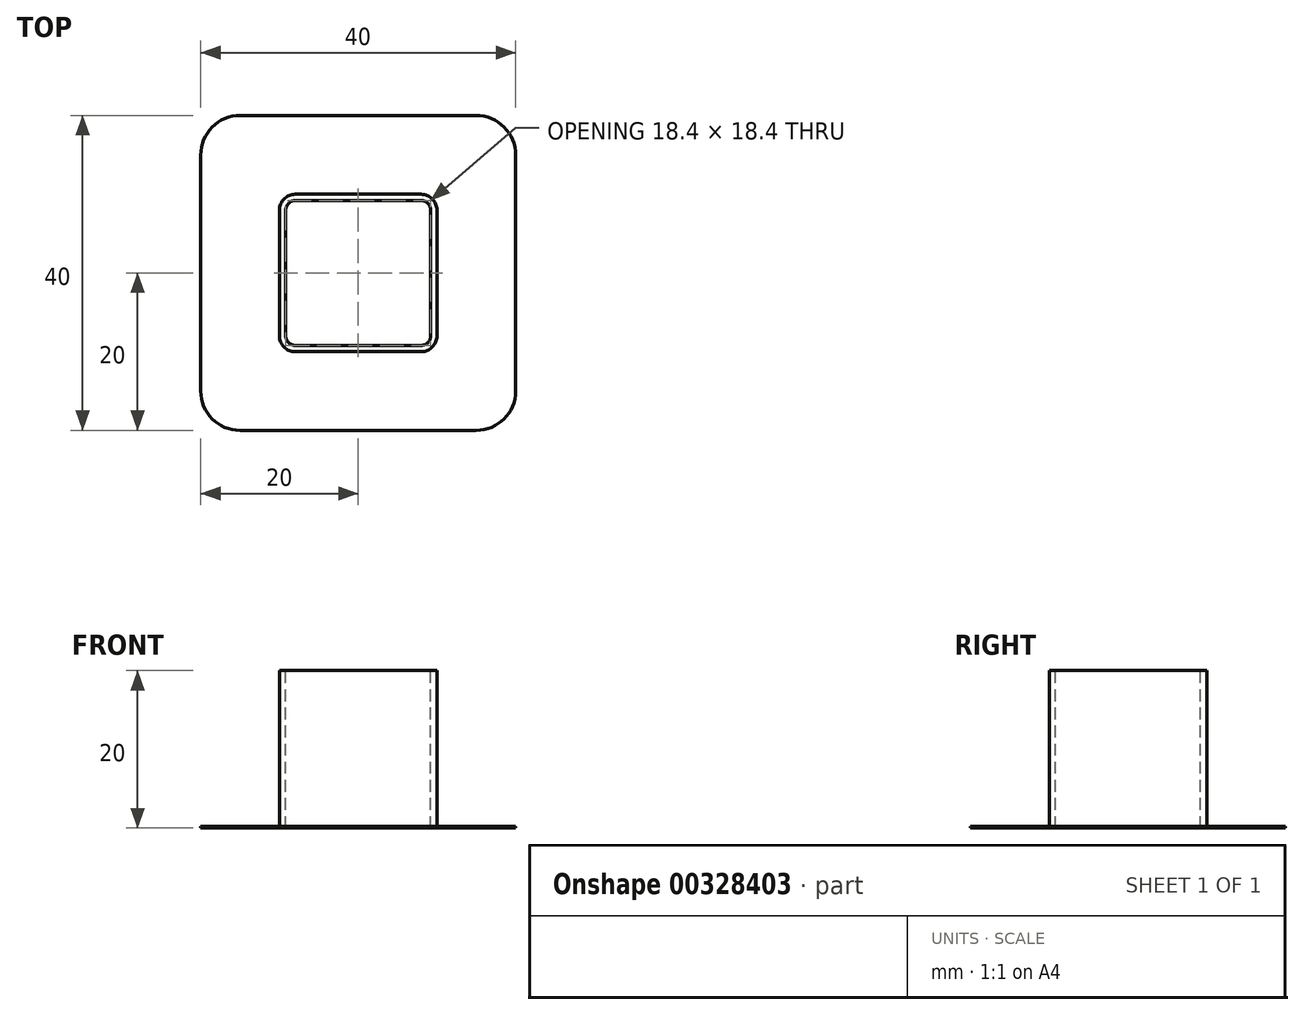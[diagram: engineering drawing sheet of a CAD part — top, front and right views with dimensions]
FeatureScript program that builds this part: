
annotation { "Feature Type Name" : "Feature", "Feature Type Description" : "" }
export const myFeature = defineFeature(function(context is Context, id is Id, definition is map)
    precondition{}
    {
        {
            var Q0;
            Q0=qCreatedBy(makeId("Top.planeOp"),FACE);
            var sketch = newSketch(context, id + "F0", { "sketchPlane" : qUnion([Q0])});
            skLineSegment(sketch, "E0.bottom", {"start": v(-8, 10) * mm, "end": v(8, 10) * mm});
            skLineSegment(sketch, "E0.top", {"start": v(-8, -10) * mm, "end": v(8, -10) * mm});
            skLineSegment(sketch, "E0.left", {"start": v(-10, 8) * mm, "end": v(-10, -8) * mm});
            skLineSegment(sketch, "E0.right", {"start": v(10, 8) * mm, "end": v(10, -8) * mm});
            skPoint(sketch, "E1", {"position": v(0, 10) * mm});
            skPoint(sketch, "E2", {"position": v(10, 0) * mm});
            skPoint(sketch, "E3.visualSharp", {"position": v(-10, 10) * mm});
            skArc(sketch, "E3.filletArc", {"start": v(-8, 10) * mm, "mid": v(-9.41, 9.41) * mm, "end": v(-10, 8) * mm});
            skPoint(sketch, "E4.visualSharp", {"position": v(10, 10) * mm});
            skArc(sketch, "E4.filletArc", {"start": v(10, 8) * mm, "mid": v(9.41, 9.41) * mm, "end": v(8, 10) * mm});
            skPoint(sketch, "E5.visualSharp", {"position": v(10, -10) * mm});
            skArc(sketch, "E5.filletArc", {"start": v(8, -10) * mm, "mid": v(9.41, -9.41) * mm, "end": v(10, -8) * mm});
            skPoint(sketch, "E6.visualSharp", {"position": v(-10, -10) * mm});
            skArc(sketch, "E6.filletArc", {"start": v(-10, -8) * mm, "mid": v(-9.41, -9.41) * mm, "end": v(-8, -10) * mm});
            skSolve(sketch);
        }
        {
            var Q0;
            Q0=makeQuery(id+"F0.imprint","IMPRINT",FACE,{"disambiguationData":[TD([[makeQuery(id+"F0.imprint","IMPRINT",EDGE,{"derivedFrom":sQuery(id+"F0.wireOp",EDGE,"E0.bottom")}),-1.0]])]});
            extrude(context, id + "F1", {"entities" : qUnion([Q0]), "depth" : 20 * mm});
        }
        {
            var Q0;
            Q0=makeQuery(id+"F1.opExtrude","CAP_FACE",FACE,{"disambiguationData":[OSD([sQuery(id+"F0.wireOp",EDGE,"E0.bottom"),sQuery(id+"F0.wireOp",EDGE,"E0.top"),sQuery(id+"F0.wireOp",EDGE,"E0.left"),sQuery(id+"F0.wireOp",EDGE,"E0.right"),sQuery(id+"F0.wireOp",EDGE,"E3.filletArc"),sQuery(id+"F0.wireOp",EDGE,"E4.filletArc"),sQuery(id+"F0.wireOp",EDGE,"E5.filletArc"),sQuery(id+"F0.wireOp",EDGE,"E6.filletArc")])],"isStart":true});
            var sketch = newSketch(context, id + "F2", { "sketchPlane" : qUnion([Q0])});
            skLineSegment(sketch, "E7.bottom", {"start": v(-15, 20) * mm, "end": v(15, 20) * mm});
            skLineSegment(sketch, "E7.top", {"start": v(-15, -20) * mm, "end": v(15, -20) * mm});
            skLineSegment(sketch, "E7.left", {"start": v(-20, 15) * mm, "end": v(-20, -15) * mm});
            skLineSegment(sketch, "E7.right", {"start": v(20, 15) * mm, "end": v(20, -15) * mm});
            skPoint(sketch, "E8", {"position": v(20, 0) * mm});
            skPoint(sketch, "E9", {"position": v(0, 20) * mm});
            skPoint(sketch, "E10.visualSharp", {"position": v(-20, 20) * mm});
            skArc(sketch, "E10.filletArc", {"start": v(-15, 20) * mm, "mid": v(-18.54, 18.54) * mm, "end": v(-20, 15) * mm});
            skPoint(sketch, "E11.visualSharp", {"position": v(20, 20) * mm});
            skArc(sketch, "E11.filletArc", {"start": v(20, 15) * mm, "mid": v(18.54, 18.54) * mm, "end": v(15, 20) * mm});
            skPoint(sketch, "E12.visualSharp", {"position": v(20, -20) * mm});
            skArc(sketch, "E12.filletArc", {"start": v(15, -20) * mm, "mid": v(18.54, -18.54) * mm, "end": v(20, -15) * mm});
            skPoint(sketch, "E13.visualSharp", {"position": v(-20, -20) * mm});
            skArc(sketch, "E13.filletArc", {"start": v(-20, -15) * mm, "mid": v(-18.54, -18.54) * mm, "end": v(-15, -20) * mm});
            skSolve(sketch);
        }
        {
            var Q0;
            Q0=makeQuery(id+"F2.imprint","IMPRINT",FACE,{"disambiguationData":[TD([[makeQuery(id+"F2.imprint","IMPRINT",EDGE,{"derivedFrom":sQuery(id+"F2.wireOp",EDGE,"E7.bottom")}),-1.0]])]});
            extrude(context, id + "F3", {"entities" : qUnion([Q0]), "operationType" : NewBodyOperationType.ADD, "oppositeDirection" : true, "depth" : 0.2 * mm, "offsetDistance" : 25 * mm});
        }
        {
            var Q0;
            Q0=makeQuery(id+"F1.opExtrude","CAP_FACE",FACE,{"disambiguationData":[OSD([sQuery(id+"F0.wireOp",EDGE,"E0.bottom"),sQuery(id+"F0.wireOp",EDGE,"E0.top"),sQuery(id+"F0.wireOp",EDGE,"E0.left"),sQuery(id+"F0.wireOp",EDGE,"E0.right"),sQuery(id+"F0.wireOp",EDGE,"E3.filletArc"),sQuery(id+"F0.wireOp",EDGE,"E4.filletArc"),sQuery(id+"F0.wireOp",EDGE,"E5.filletArc"),sQuery(id+"F0.wireOp",EDGE,"E6.filletArc")])],"isStart":false});
            var sketch = newSketch(context, id + "F4", { "sketchPlane" : qUnion([Q0])});
            skLineSegment(sketch, "E14.0", {"start": v(-9.2, 8) * mm, "end": v(-9.2, -8) * mm});
            skArc(sketch, "E14.1", {"start": v(-8, 9.2) * mm, "mid": v(-8.85, 8.85) * mm, "end": v(-9.2, 8) * mm});
            skArc(sketch, "E14.2", {"start": v(-9.2, -8) * mm, "mid": v(-8.85, -8.85) * mm, "end": v(-8, -9.2) * mm});
            skLineSegment(sketch, "E14.3", {"start": v(8, 9.2) * mm, "end": v(-8, 9.2) * mm});
            skLineSegment(sketch, "E14.4", {"start": v(-8, -9.2) * mm, "end": v(8, -9.2) * mm});
            skArc(sketch, "E14.5", {"start": v(8, -9.2) * mm, "mid": v(8.85, -8.85) * mm, "end": v(9.2, -8) * mm});
            skLineSegment(sketch, "E14.6", {"start": v(9.2, -8) * mm, "end": v(9.2, 8) * mm});
            skArc(sketch, "E14.7", {"start": v(9.2, 8) * mm, "mid": v(8.85, 8.85) * mm, "end": v(8, 9.2) * mm});
            skSolve(sketch);
        }
        {
            var Q0;
            Q0=makeQuery(id+"F4.imprint","IMPRINT",FACE,{"disambiguationData":[TD([[makeQuery(id+"F4.imprint","IMPRINT",EDGE,{"derivedFrom":sQuery(id+"F4.wireOp",EDGE,"E14.0")}),1.0]])]});
            var Q1;
            Q1=makeQuery(id+"F3.opExtrude","CAP_FACE",FACE,{"disambiguationData":[OSD([sQuery(id+"F0.wireOp",EDGE,"E0.bottom"),sQuery(id+"F0.wireOp",EDGE,"E0.top"),sQuery(id+"F0.wireOp",EDGE,"E0.left"),sQuery(id+"F0.wireOp",EDGE,"E0.right"),sQuery(id+"F0.wireOp",EDGE,"E3.filletArc"),sQuery(id+"F0.wireOp",EDGE,"E4.filletArc"),sQuery(id+"F0.wireOp",EDGE,"E5.filletArc"),sQuery(id+"F0.wireOp",EDGE,"E6.filletArc"),sQuery(id+"F2.wireOp",EDGE,"E7.bottom"),sQuery(id+"F2.wireOp",EDGE,"E7.top"),sQuery(id+"F2.wireOp",EDGE,"E7.left"),sQuery(id+"F2.wireOp",EDGE,"E7.right"),sQuery(id+"F2.wireOp",EDGE,"E10.filletArc"),sQuery(id+"F2.wireOp",EDGE,"E11.filletArc"),sQuery(id+"F2.wireOp",EDGE,"E12.filletArc"),sQuery(id+"F2.wireOp",EDGE,"E13.filletArc")])],"isStart":false});
            extrude(context, id + "F5", {"entities" : qUnion([Q0]), "operationType" : NewBodyOperationType.REMOVE, "endBound" : BoundingType.THROUGH_ALL, "oppositeDirection" : true, "depth" : 25 * mm, "endBoundEntityFace" : qUnion([Q1]), "offsetDistance" : 25 * mm});
        }
    });
